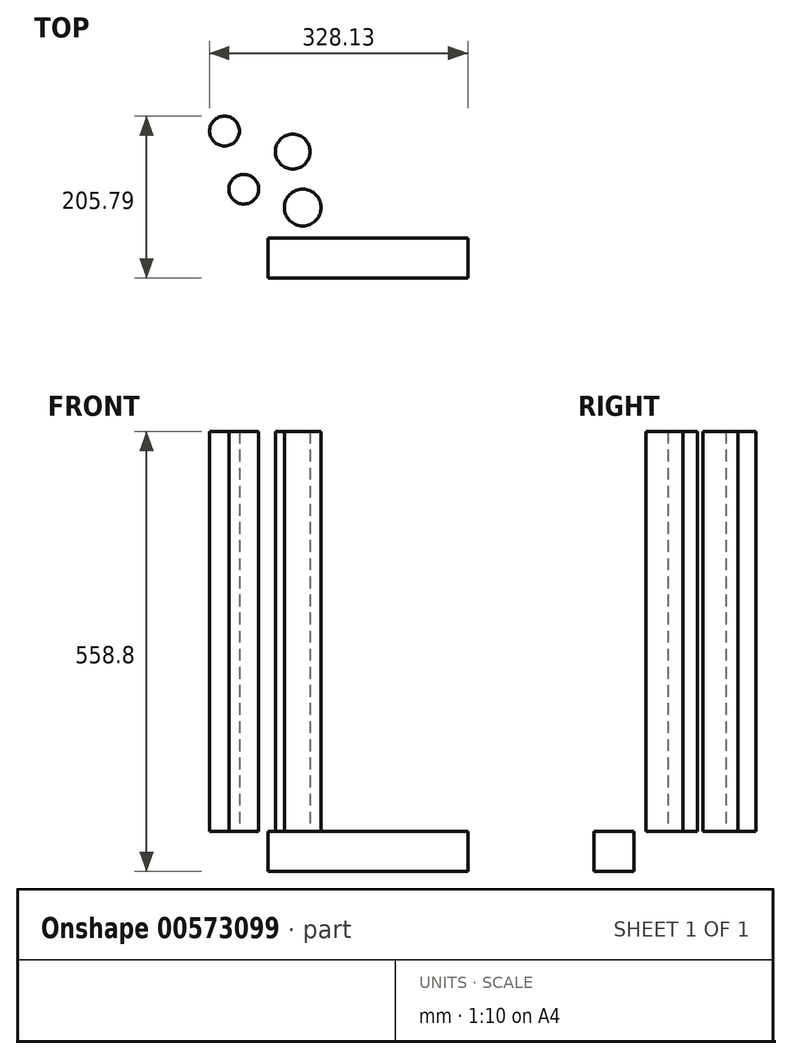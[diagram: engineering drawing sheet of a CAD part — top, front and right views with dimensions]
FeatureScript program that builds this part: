
annotation { "Feature Type Name" : "Feature", "Feature Type Description" : "" }
export const myFeature = defineFeature(function(context is Context, id is Id, definition is map)
    precondition{}
    {
        {
            var Q0;
            Q0=qCreatedBy(makeId("Top.planeOp"),FACE);
            var sketch = newSketch(context, id + "F0", { "sketchPlane" : qUnion([Q0])});
            skCircle(sketch, "E0", {"center": v(-30.71, -28.06) * mm, "radius": 18.85 * mm});
            skCircle(sketch, "E1", {"center": v(31.47, 19.72) * mm, "radius": 22.1 * mm});
            skCircle(sketch, "E2", {"center": v(-55.17, 45.88) * mm, "radius": 18.96 * mm});
            skCircle(sketch, "E3", {"center": v(44.18, -51.38) * mm, "radius": 23.35 * mm});
            skSolve(sketch);
        }
        {
            var Q0;
            Q0=makeQuery(id+"F0.imprint","IMPRINT",FACE,{"disambiguationData":[TD([[makeQuery(id+"F0.imprint","IMPRINT",EDGE,{"derivedFrom":sQuery(id+"F0.wireOp",EDGE,"E2")}),1.0]])]});
            var Q1;
            Q1=makeQuery(id+"F0.imprint","IMPRINT",FACE,{"disambiguationData":[TD([[makeQuery(id+"F0.imprint","IMPRINT",EDGE,{"derivedFrom":sQuery(id+"F0.wireOp",EDGE,"E0")}),1.0]])]});
            var Q2;
            Q2=makeQuery(id+"F0.imprint","IMPRINT",FACE,{"disambiguationData":[TD([[makeQuery(id+"F0.imprint","IMPRINT",EDGE,{"derivedFrom":sQuery(id+"F0.wireOp",EDGE,"E1")}),1.0]])]});
            var Q3;
            Q3=makeQuery(id+"F0.imprint","IMPRINT",FACE,{"disambiguationData":[TD([[makeQuery(id+"F0.imprint","IMPRINT",EDGE,{"derivedFrom":sQuery(id+"F0.wireOp",EDGE,"E3")}),1.0]])]});
            extrude(context, id + "F1", {"entities" : qUnion([Q0, Q1, Q2, Q3]), "depth" : 508 * mm, "offsetDistance" : 25.4 * mm});
        }
        {
            var Q0;
            Q0=qCreatedBy(makeId("Right.planeOp"),FACE);
            var sketch = newSketch(context, id + "F2", { "sketchPlane" : qUnion([Q0])});
            skLineSegment(sketch, "E4.bottom", {"start": v(-140.95, 0) * mm, "end": v(-90.15, 0) * mm});
            skLineSegment(sketch, "E4.top", {"start": v(-140.95, -50.8) * mm, "end": v(-90.15, -50.8) * mm});
            skLineSegment(sketch, "E4.left", {"start": v(-140.95, 0) * mm, "end": v(-140.95, -50.8) * mm});
            skLineSegment(sketch, "E4.right", {"start": v(-90.15, 0) * mm, "end": v(-90.15, -50.8) * mm});
            skSolve(sketch);
        }
        {
            var Q0;
            Q0=makeQuery(id+"F2.imprint","IMPRINT",FACE,{"disambiguationData":[TD([[makeQuery(id+"F2.imprint","IMPRINT",EDGE,{"derivedFrom":sQuery(id+"F2.wireOp",EDGE,"E4.bottom")}),-1.0]])]});
            extrude(context, id + "F3", {"entities" : qUnion([Q0]), "depth" : 254 * mm, "offsetDistance" : 25.4 * mm});
        }
    });
